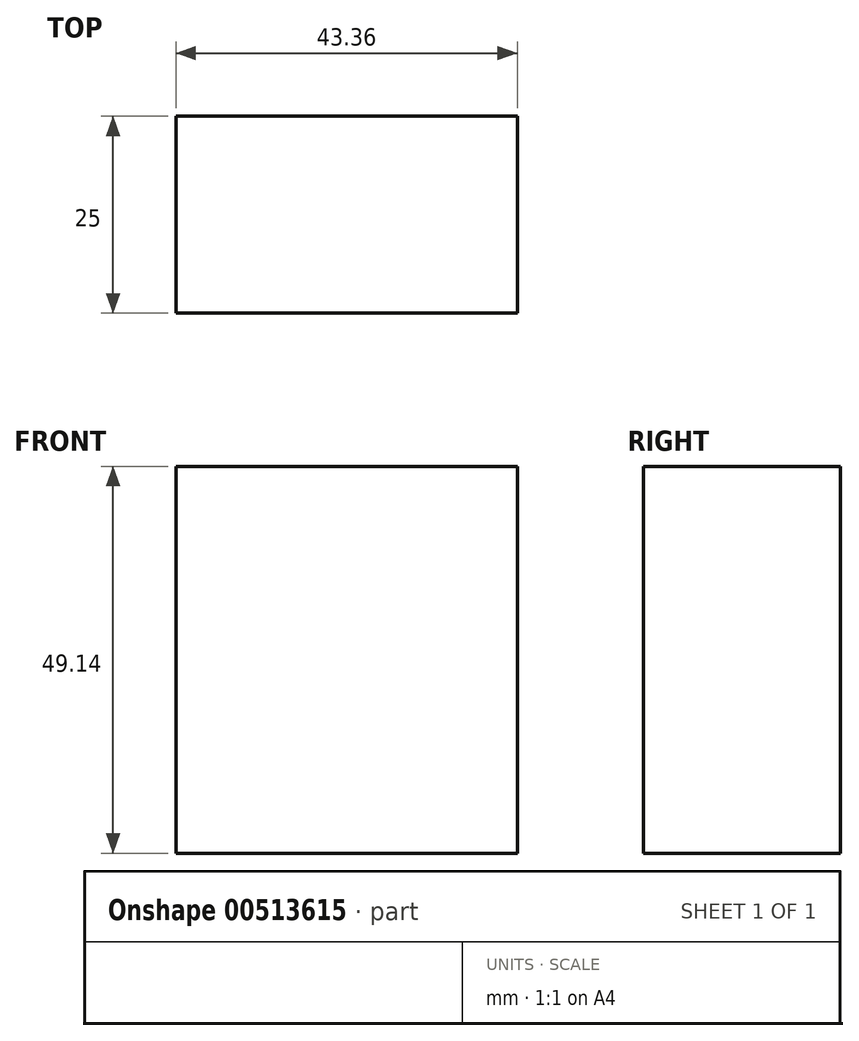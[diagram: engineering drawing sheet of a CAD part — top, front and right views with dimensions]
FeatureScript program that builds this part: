
annotation { "Feature Type Name" : "Feature", "Feature Type Description" : "" }
export const myFeature = defineFeature(function(context is Context, id is Id, definition is map)
    precondition{}
    {
        {
            var Q0;
            Q0=qCreatedBy(makeId("Front.planeOp"),FACE);
            var sketch = newSketch(context, id + "F0", { "sketchPlane" : qUnion([Q0])});
            skLineSegment(sketch, "E0.bottom", {"start": v(-150.32, -9.25) * mm, "end": v(-106.96, -9.25) * mm});
            skLineSegment(sketch, "E0.top", {"start": v(-150.32, 39.9) * mm, "end": v(-106.96, 39.9) * mm});
            skLineSegment(sketch, "E0.left", {"start": v(-150.32, -9.25) * mm, "end": v(-150.32, 39.9) * mm});
            skLineSegment(sketch, "E0.right", {"start": v(-106.96, -9.25) * mm, "end": v(-106.96, 39.9) * mm});
            skPoint(sketch, "E0.middle", {"position": v(-128.64, 15.32) * mm});
            skSolve(sketch);
        }
        {
            var Q0;
            Q0=makeQuery(id+"F0.imprint","IMPRINT",FACE,{"disambiguationData":[TD([[makeQuery(id+"F0.imprint","IMPRINT",EDGE,{"derivedFrom":sQuery(id+"F0.wireOp",EDGE,"E0.bottom")}),1.0]])]});
            extrude(context, id + "F1", {"entities" : qUnion([Q0]), "depth" : 25 * mm});
        }
        {
            var Q0;
            Q0=makeQuery(id+"F1.opExtrude","CAP_FACE",FACE,{"disambiguationData":[OSD([sQuery(id+"F0.wireOp",EDGE,"E0.bottom"),sQuery(id+"F0.wireOp",EDGE,"E0.top"),sQuery(id+"F0.wireOp",EDGE,"E0.left"),sQuery(id+"F0.wireOp",EDGE,"E0.right")])],"isStart":false});
            cPlane(context, id + "F2", {"entities" : qUnion([Q0]), "cplaneType" : CPlaneType.OFFSET, "offset" : 25 * mm, "width" : 150 * mm, "height" : 150 * mm});
        }
    });
